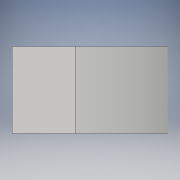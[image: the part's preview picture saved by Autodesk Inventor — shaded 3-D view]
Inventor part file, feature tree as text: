
AUTODESK INVENTOR PART (.ipt)
format: ipt  version: 2018.2 (Build 222227000, 227)  size: 94,208 bytes
history: native  units: mm
features: other x1, extrude x1, sketch x1
ambient origin geometry x8: Origin, YZ Plane, XZ Plane, XY Plane, X Axis, Y Axis, Z Axis, Center Point
bodies: Body1 (feature_tree)
feature tree (3):
  other  "ソリッド1"
  extrude  "押し出し1"  Depth=3000.0mm
  sketch  "スケッチ1"
